# Revit family: 03_CMP_FD312_PB1A
name_source: partatom
category: Porte
units: mm (PartAtom-declared; Revit-internal decimal feet)

## family parameters
Condiviso = No
Host = Muro
Numero OmniClass = 23.30.10.00
Punto di calcolo locali = Sì
Sempre verticale = Sì
Taglio con vuoti quando caricato = No
Titolo OmniClass = Doors

## types (3) — shared parameters
Altezza = 2100 mm  [stored 6.88976 ft]
Chiusura muro = Per host
Codice assieme = B2030100
Costruzione analitica = <Nessuno>
EXTERNAL ALUMINUM FRAME/TELAIO ALLUMINIO ESTERNO = UNIFORM_ALUMINUM
Funzione = Interno
H = 2100 mm  [stored 6.88976 ft]
HANDLE HEIGHT/ALTEZZA MANIGLIA = 1100 mm
HANDLE/MANIGLIA = UNIFORM_ALUMINUM
HOLE_H = 2100 mm  [stored 6.88976 ft]
HOLE_W = 1000 mm  [stored 3.28084 ft]
HTI = 2085 mm  [stored 6.84055 ft]
INTERIOR WOOD FRAME/TELAIO LEGNO INTERNO = UNIFORM_WOOD
Immagine tipo = <Nessuno>
Larghezza = 1000 mm  [stored 3.28084 ft]
Larghezza telaio = 75 mm
MAX_DIMENSIONS_WARNING = No
MINIMUM HEIGHT/ALTEZZA MINIMA = 1800 mm  [stored 5.90551 ft]
MINIMUM WIDTH/LARGHEZZA MINIMA  = 500 mm  [stored 1.64042 ft]
Modello = COMPLANARE
PRODUCER WEBSITE/SITO WEB PRODUTTORE = www.uniform.it
PRODUCT WEBSITE/SITO WEB PRODOTTO = www.sistema-uni-one.it
Produttore = UNIFORM
Proiezione telaio est. = 25 mm  [stored 0.082021 ft]
Proiezione telaio int. = 25 mm  [stored 0.082021 ft]
URL = https://www.sistema-uni-one.it
W = 1000 mm  [stored 3.28084 ft]
WINDOW GLASS/VETRO FINESTRA = UNIFORM_GLASS
WINDOW SILL/BANCALINO FINESTRA = UNIFORM_STONE
zero-valued in all types: T_F_H, WINDOW HOLE TOLERANCE/TOLLERANZA FORO FINESTRA

## per-type parameters (varying)
| type | GLASS WEIGHT/PESO VETRO | MAXIMUM HEIGHT/ALTEZZA MASSIMA | MAXIMUM WIDTH/LARGHEZZA MASSIMA | Rw GLASS/Rw VETRO | Rw WINDOW/Rw FINESTRA | Ug GLASS/Ug VETRO | Uw WINDOW/Uw FINESTRA |
| PB1A_ACOUSTICS | 60.00 kg/m² | 2400 mm | 1800 mm  [stored 5.90551 ft] | 49 | 43 | 1.1000 W/(m²·K) | 1.3000 W/(m²·K) |
| PB1A_THERMAL | 43.00 kg/m² | 2500 mm | 1000 mm  [stored 3.28084 ft] | 0 | 0 | 1.0000 W/(m²·K) | 1.2000 W/(m²·K) |
| PB1A_HIGH THERMAL PERFORMANCE | 43.00 kg/m² | 2500 mm | 1000 mm  [stored 3.28084 ft] | 0 | 0 | 0.5000 W/(m²·K) | 0.8000 W/(m²·K) |

note: [stored X ft] marks values corroborated as IEEE doubles in the binary element streams (Revit-internal decimal feet)
